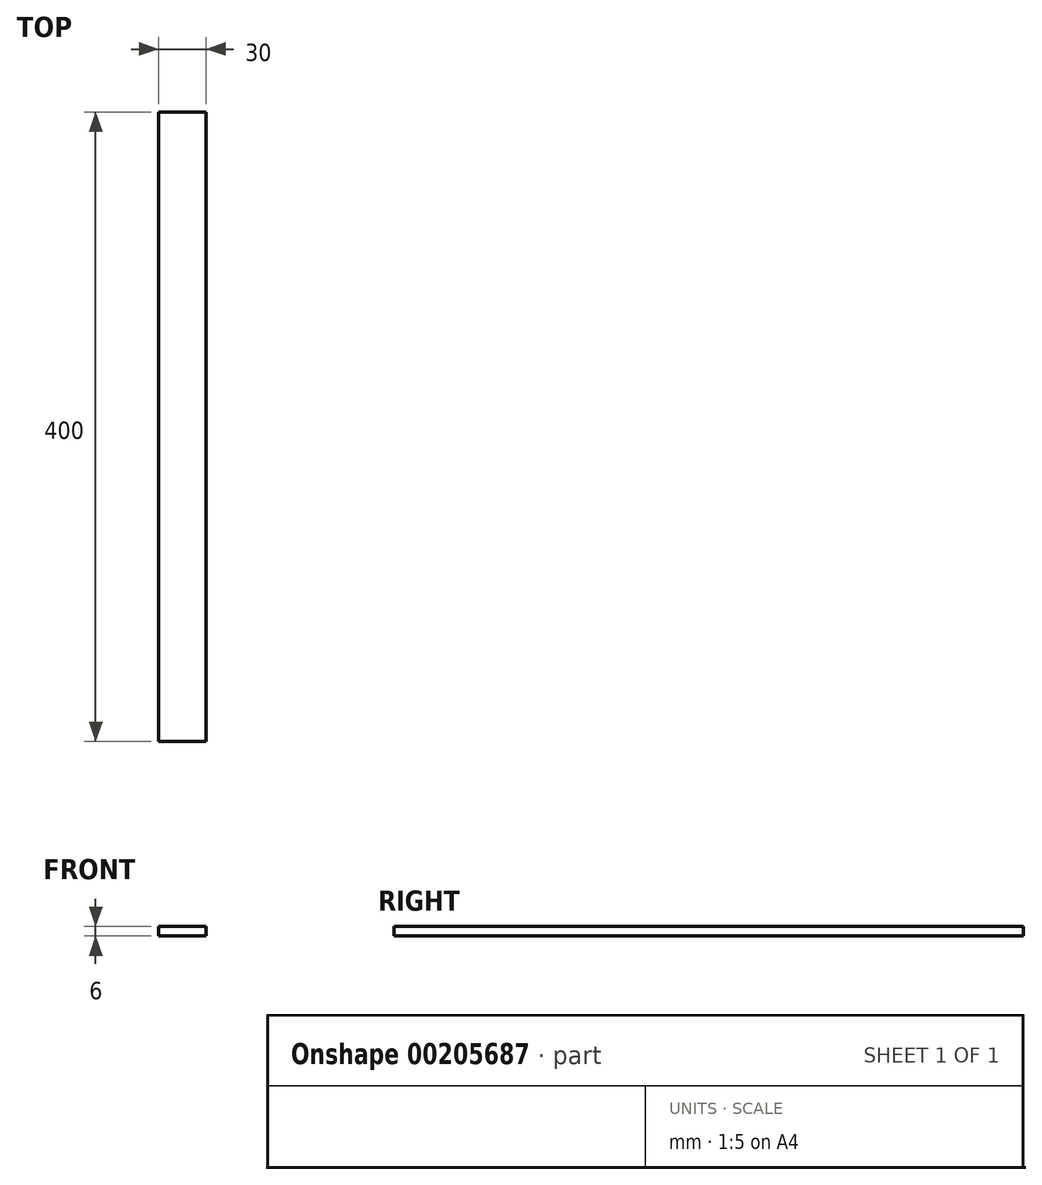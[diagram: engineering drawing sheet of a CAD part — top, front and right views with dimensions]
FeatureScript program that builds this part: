
annotation { "Feature Type Name" : "Feature", "Feature Type Description" : "" }
export const myFeature = defineFeature(function(context is Context, id is Id, definition is map)
    precondition{}
    {
        {
            var Q0;
            Q0=qCreatedBy(makeId("Top.planeOp"),FACE);
            var sketch = newSketch(context, id + "F0", { "sketchPlane" : qUnion([Q0])});
            skLineSegment(sketch, "E0.bottom", {"start": v(-76.12, 351.91) * mm, "end": v(-46.12, 351.91) * mm});
            skLineSegment(sketch, "E0.top", {"start": v(-76.12, -48.09) * mm, "end": v(-46.12, -48.09) * mm});
            skLineSegment(sketch, "E0.left", {"start": v(-76.12, 351.91) * mm, "end": v(-76.12, -48.09) * mm});
            skLineSegment(sketch, "E0.right", {"start": v(-46.12, 351.91) * mm, "end": v(-46.12, -48.09) * mm});
            skSolve(sketch);
        }
        {
            var Q0;
            Q0 = qSketchRegion(id + "F0", true);
            extrude(context, id + "F1", {"entities" : qUnion([Q0]), "depth" : 6 * mm});
        }
    });
